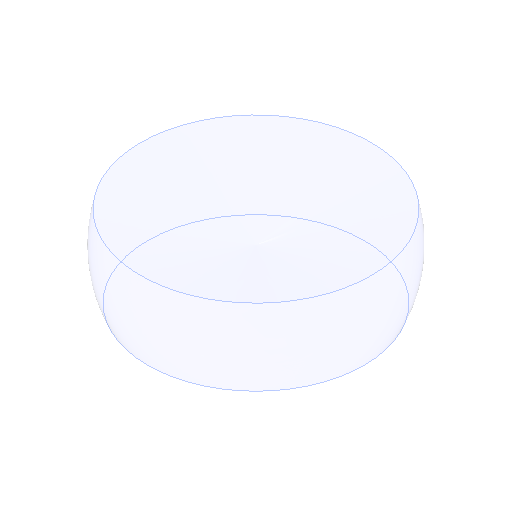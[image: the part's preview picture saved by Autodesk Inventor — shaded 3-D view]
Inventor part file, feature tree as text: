
AUTODESK INVENTOR PART (.ipt)
format: ipt  version: 2025 (Build 290162000, 162)  size: 122,880 bytes
history: native  units: mm
features: revolve x1, sketch x1
ambient origin geometry x8: Origin, YZ Plane, XZ Plane, XY Plane, X Axis, Y Axis, Z Axis, Center Point
bodies: Solid1 (feature_tree)
feature tree (2):
  revolve  "Revolution1"  Angle=15.0deg
  sketch  "Sketch1"  dims[d0=2000.0mm d1=15.0deg d2=4.363323mm d3=90.0deg]
